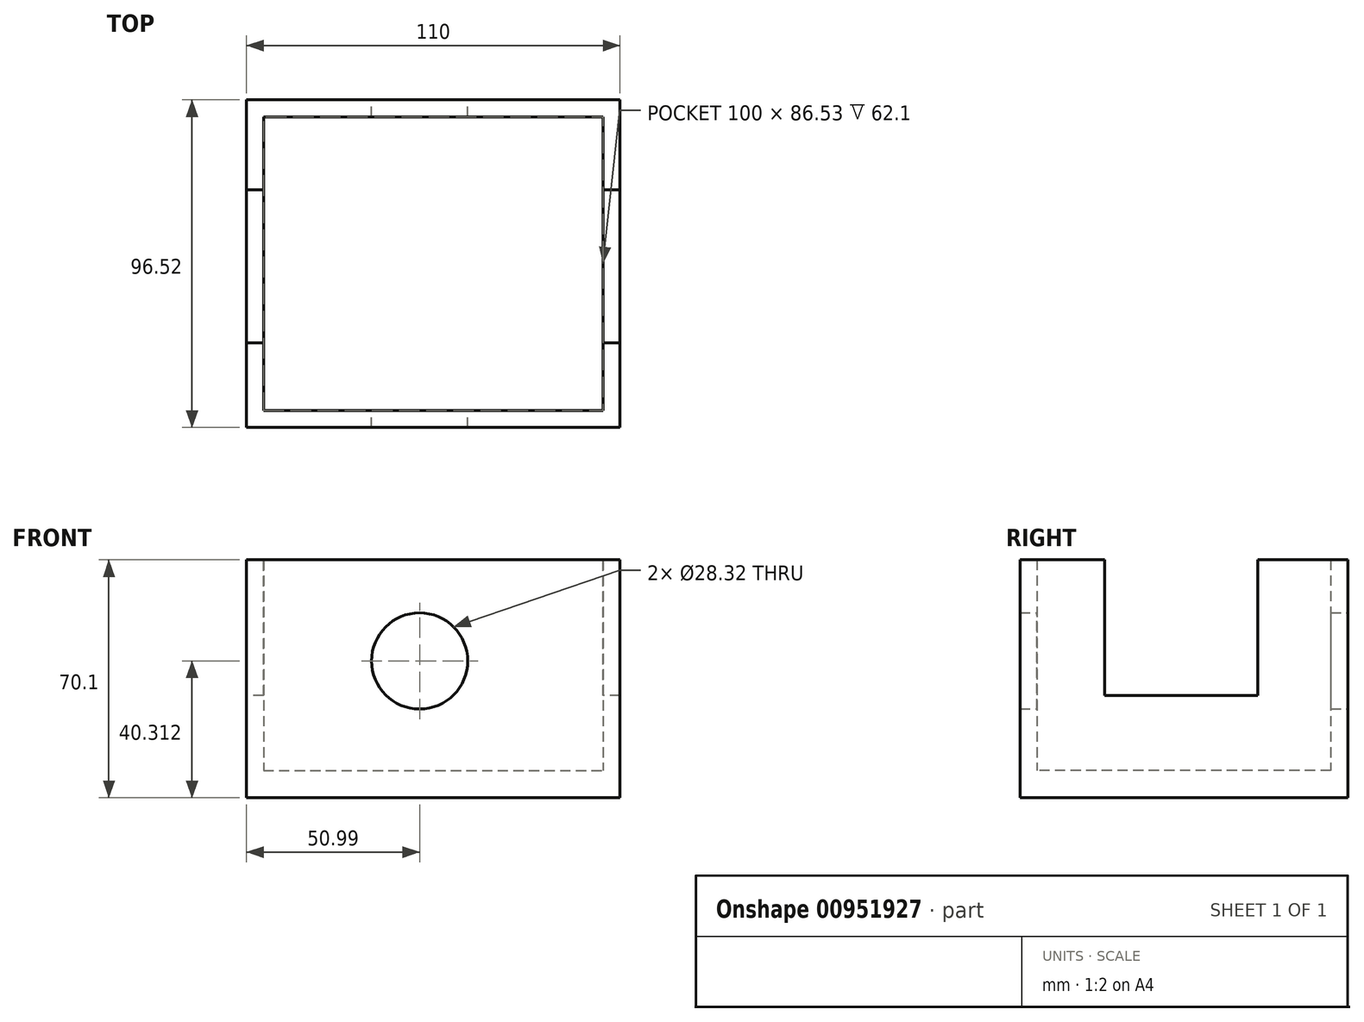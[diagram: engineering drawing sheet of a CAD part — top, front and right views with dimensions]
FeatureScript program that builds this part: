
annotation { "Feature Type Name" : "Feature", "Feature Type Description" : "" }
export const myFeature = defineFeature(function(context is Context, id is Id, definition is map)
    precondition{}
    {
        {
            var Q0;
            Q0=qCreatedBy(makeId("Top.planeOp"),FACE);
            var sketch = newSketch(context, id + "F0", { "sketchPlane" : qUnion([Q0])});
            skLineSegment(sketch, "E0.bottom", {"start": v(-51, -21.74) * mm, "end": v(59, -21.74) * mm});
            skLineSegment(sketch, "E0.top", {"start": v(-51, 48.26) * mm, "end": v(59, 48.26) * mm});
            skLineSegment(sketch, "E0.left", {"start": v(-51, -21.74) * mm, "end": v(-51, 48.26) * mm});
            skLineSegment(sketch, "E0.right", {"start": v(59, -21.74) * mm, "end": v(59, 48.26) * mm});
            skSolve(sketch);
        }
        {
            var Q0;
            Q0=makeQuery(id+"F0.imprint","IMPRINT",FACE,{"disambiguationData":[TD([[makeQuery(id+"F0.imprint","IMPRINT",EDGE,{"derivedFrom":sQuery(id+"F0.wireOp",EDGE,"E0.bottom")}),1.0]])]});
            extrude(context, id + "F1", {"entities" : qUnion([Q0]), "depth" : 8 * mm, "offsetDistance" : 25 * mm});
        }
        {
            var Q0;
            Q0=makeQuery(id+"F1.opExtrude","CAP_FACE",FACE,{"disambiguationData":[OSD([sQuery(id+"F0.wireOp",EDGE,"E0.bottom"),sQuery(id+"F0.wireOp",EDGE,"E0.top"),sQuery(id+"F0.wireOp",EDGE,"E0.left"),sQuery(id+"F0.wireOp",EDGE,"E0.right")])],"isStart":false});
            var sketch = newSketch(context, id + "F2", { "sketchPlane" : qUnion([Q0])});
            skLineSegment(sketch, "E1.bottom", {"start": v(-51, 48.26) * mm, "end": v(59, 48.26) * mm});
            skLineSegment(sketch, "E1.top", {"start": v(-51, 43.26) * mm, "end": v(59, 43.26) * mm});
            skLineSegment(sketch, "E1.left", {"start": v(-51, 48.26) * mm, "end": v(-51, 43.26) * mm});
            skLineSegment(sketch, "E1.right", {"start": v(59, 48.26) * mm, "end": v(59, 43.26) * mm});
            skLineSegment(sketch, "E2.bottom", {"start": v(-51, 43.26) * mm, "end": v(-46, 43.26) * mm});
            skLineSegment(sketch, "E2.top", {"start": v(-51, 3.26) * mm, "end": v(-46, 3.26) * mm});
            skLineSegment(sketch, "E2.left", {"start": v(-51, 43.26) * mm, "end": v(-51, 3.26) * mm});
            skLineSegment(sketch, "E2.right", {"start": v(-46, 43.26) * mm, "end": v(-46, 3.26) * mm});
            skLineSegment(sketch, "E3.bottom", {"start": v(59, 43.26) * mm, "end": v(54, 43.26) * mm});
            skLineSegment(sketch, "E3.top", {"start": v(59, 3.26) * mm, "end": v(54, 3.26) * mm});
            skLineSegment(sketch, "E3.left", {"start": v(59, 43.26) * mm, "end": v(59, 3.26) * mm});
            skLineSegment(sketch, "E3.right", {"start": v(54, 43.26) * mm, "end": v(54, 3.26) * mm});
            skLineSegment(sketch, "E4.top", {"start": v(-51, -21.74) * mm, "end": v(-46, -21.74) * mm});
            skLineSegment(sketch, "E4.left", {"start": v(-51, 3.26) * mm, "end": v(-51, -21.74) * mm});
            skLineSegment(sketch, "E4.right", {"start": v(-46, 3.26) * mm, "end": v(-46, -21.74) * mm});
            skLineSegment(sketch, "E5.bottom", {"start": v(54, 3.26) * mm, "end": v(59, 3.26) * mm});
            skLineSegment(sketch, "E5.top", {"start": v(54, -21.74) * mm, "end": v(59, -21.74) * mm});
            skLineSegment(sketch, "E5.left", {"start": v(54, 3.26) * mm, "end": v(54, -21.74) * mm});
            skLineSegment(sketch, "E5.right", {"start": v(59, 3.26) * mm, "end": v(59, -21.74) * mm});
            skSolve(sketch);
        }
        {
            var Q0;
            Q0 = qSketchRegion(id + "F2", true);
            extrude(context, id + "F3", {"entities" : qUnion([Q0]), "operationType" : NewBodyOperationType.ADD, "depth" : 62.1 * mm, "offsetDistance" : 25 * mm});
        }
        {
            var Q0;
            Q0=makeQuery(id+"F3.boolean.opBoolean","MERGE",FACE,{"derivedFrom":[makeQuery(id+"F1.opExtrude","SWEPT_FACE",FACE,{"disambiguationData":[OSD([sQuery(id+"F0.wireOp",EDGE,"E0.left")])]}),makeQuery(id+"F3.opExtrude","SWEPT_FACE",FACE,{"disambiguationData":[OSD([sQuery(id+"F2.wireOp",EDGE,"E1.left"),sQuery(id+"F2.wireOp",EDGE,"E2.left"),sQuery(id+"F2.wireOp",EDGE,"E4.left")])]})]});
            var sketch = newSketch(context, id + "F4", { "sketchPlane" : qUnion([Q0])});
            skLineSegment(sketch, "E6.bottom", {"start": v(21.74, 70.1) * mm, "end": v(-6.26, 70.1) * mm});
            skLineSegment(sketch, "E6.top", {"start": v(21.74, 30.1) * mm, "end": v(-6.26, 30.1) * mm});
            skLineSegment(sketch, "E6.left", {"start": v(21.74, 70.1) * mm, "end": v(21.74, 30.1) * mm});
            skLineSegment(sketch, "E6.right", {"start": v(-6.26, 70.1) * mm, "end": v(-6.26, 30.1) * mm});
            skSolve(sketch);
        }
        {
            var Q0;
            Q0 = qSketchRegion(id + "F4", true);
            extrude(context, id + "F5", {"entities" : qUnion([Q0]), "operationType" : NewBodyOperationType.REMOVE, "oppositeDirection" : true, "depth" : 117.8 * mm, "offsetDistance" : 25 * mm});
        }
        {
            var Q0;
            Q0=makeQuery(id+"F1.opExtrude","SWEPT_BODY",BODY,{"disambiguationData":[OSD([sQuery(id+"F0.wireOp",EDGE,"E0.bottom"),sQuery(id+"F0.wireOp",EDGE,"E0.top"),sQuery(id+"F0.wireOp",EDGE,"E0.left"),sQuery(id+"F0.wireOp",EDGE,"E0.right")])]});
            var Q1;
            Q1=qCreatedBy(makeId("Front.planeOp"),FACE);
            mirror(context, id + "F6", {"operationType" : NewBodyOperationType.ADD, "entities" : qUnion([Q0]), "mirrorPlane" : qUnion([Q1])});
        }
        {
            var Q0;
            Q0=makeQuery(id+"F5.boolean.opBoolean","COPY",FACE,{"disambiguationData":[TD([makeQuery(id+"F1.opExtrude","SWEPT_FACE",FACE,{"disambiguationData":[OSD([sQuery(id+"F0.wireOp",EDGE,"E0.left")])]})])],"derivedFrom":makeQuery(id+"F5.opExtrude","SWEPT_FACE",FACE,{"disambiguationData":[OSD([sQuery(id+"F4.wireOp",EDGE,"E6.right")])]})});
            var Q1;
            Q1=makeQuery(id+"F5.boolean.opBoolean","COPY",FACE,{"disambiguationData":[TD([makeQuery(id+"F1.opExtrude","SWEPT_FACE",FACE,{"disambiguationData":[OSD([sQuery(id+"F0.wireOp",EDGE,"E0.right")])]})])],"derivedFrom":makeQuery(id+"F5.opExtrude","SWEPT_FACE",FACE,{"disambiguationData":[OSD([sQuery(id+"F4.wireOp",EDGE,"E6.right")])]})});
            extrude(context, id + "F7", {"entities" : qUnion([Q0, Q1]), "operationType" : NewBodyOperationType.REMOVE, "oppositeDirection" : true, "depth" : 15.5 * mm, "offsetDistance" : 25 * mm});
        }
        {
            var Q0;
            Q0=makeQuery(id+"F6.opPattern","COPY",FACE,{"derivedFrom":makeQuery(id+"F5.boolean.opBoolean","COPY",FACE,{"disambiguationData":[TD([makeQuery(id+"F1.opExtrude","SWEPT_FACE",FACE,{"disambiguationData":[OSD([sQuery(id+"F0.wireOp",EDGE,"E0.right")])]})])],"derivedFrom":makeQuery(id+"F5.opExtrude","SWEPT_FACE",FACE,{"disambiguationData":[OSD([sQuery(id+"F4.wireOp",EDGE,"E6.right")])]})}),"instanceName":"1"});
            var Q1;
            Q1=makeQuery(id+"F6.opPattern","COPY",FACE,{"derivedFrom":makeQuery(id+"F5.boolean.opBoolean","COPY",FACE,{"disambiguationData":[TD([makeQuery(id+"F1.opExtrude","SWEPT_FACE",FACE,{"disambiguationData":[OSD([sQuery(id+"F0.wireOp",EDGE,"E0.left")])]})])],"derivedFrom":makeQuery(id+"F5.opExtrude","SWEPT_FACE",FACE,{"disambiguationData":[OSD([sQuery(id+"F4.wireOp",EDGE,"E6.right")])]})}),"instanceName":"1"});
            extrude(context, id + "F8", {"entities" : qUnion([Q0, Q1]), "operationType" : NewBodyOperationType.REMOVE, "oppositeDirection" : true, "depth" : 17 * mm, "offsetDistance" : 25 * mm});
        }
        {
            var Q0;
            Q0=makeQuery(id+"F3.boolean.opBoolean","MERGE",FACE,{"derivedFrom":[makeQuery(id+"F1.opExtrude","SWEPT_FACE",FACE,{"disambiguationData":[OSD([sQuery(id+"F0.wireOp",EDGE,"E0.top")])]}),makeQuery(id+"F3.opExtrude","SWEPT_FACE",FACE,{"disambiguationData":[OSD([sQuery(id+"F2.wireOp",EDGE,"E1.bottom")])]})]});
            var sketch = newSketch(context, id + "F9", { "sketchPlane" : qUnion([Q0])});
            skCircle(sketch, "E7", {"center": v(0, 40.31) * mm, "radius": 14.16 * mm});
            skSolve(sketch);
        }
        {
            var Q0;
            Q0=makeQuery(id+"F9.imprint","IMPRINT",FACE,{"disambiguationData":[TD([[makeQuery(id+"F9.imprint","IMPRINT",EDGE,{"derivedFrom":sQuery(id+"F9.wireOp",EDGE,"E7")}),1.0]])]});
            extrude(context, id + "F10", {"entities" : qUnion([Q0]), "operationType" : NewBodyOperationType.REMOVE, "endBound" : BoundingType.THROUGH_ALL, "oppositeDirection" : true, "depth" : 25 * mm, "offsetDistance" : 25 * mm});
        }
    });
